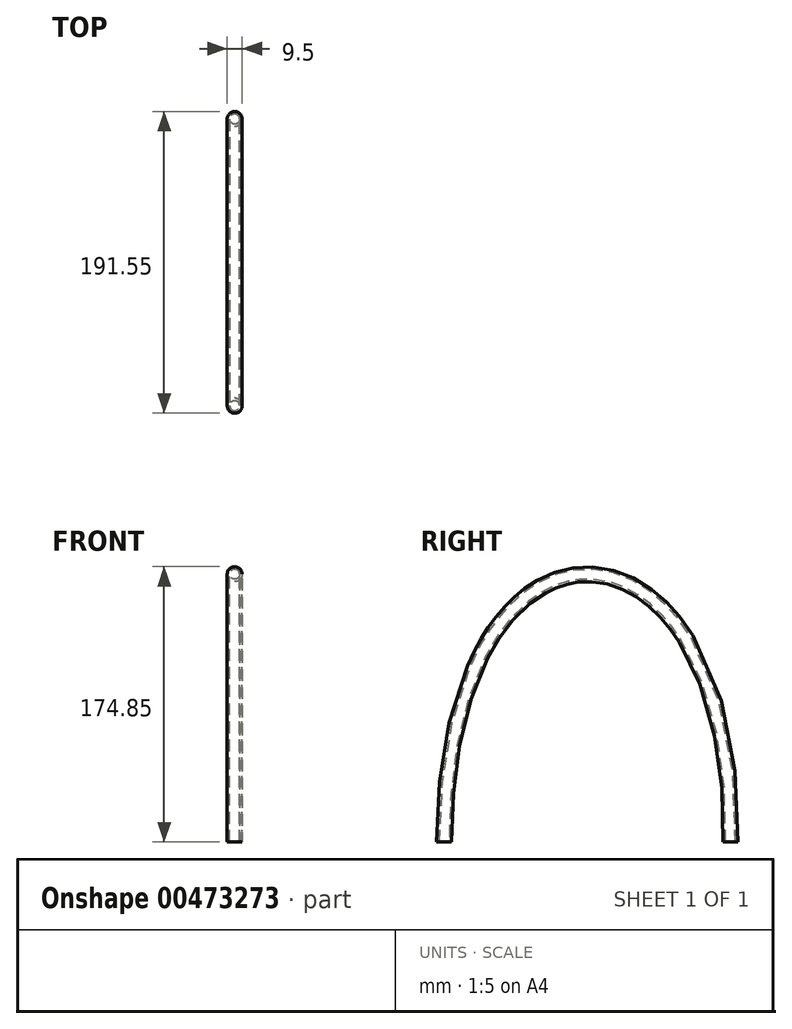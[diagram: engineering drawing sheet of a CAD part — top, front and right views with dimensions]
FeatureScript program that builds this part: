
annotation { "Feature Type Name" : "Feature", "Feature Type Description" : "" }
export const myFeature = defineFeature(function(context is Context, id is Id, definition is map)
    precondition{}
    {
        {
            var Q0;
            Q0=qCreatedBy(makeId("Top.planeOp"), FACE);
            var sketch = newSketch(context, id + "F0", { "sketchPlane" : qUnion([Q0])});
            skCircle(sketch, "E0", {"center": v(0, 0) * mm, "radius": 3.14 * mm});
            skCircle(sketch, "E1", {"center": v(0, 0) * mm, "radius": 4.75 * mm});
            skSolve(sketch);
        }
        {
            var Q0;
            Q0=qCreatedBy(makeId("Right.planeOp"), FACE);
            var sketch = newSketch(context, id + "F1", { "sketchPlane" : qUnion([Q0])});
            skPoint(sketch, "E2", {"position": v(181.97, 0) * mm});
            skFitSpline(sketch, "E3", {"points": [v(0, 0) * mm, v(181.97, 0) * mm], "startDerivative": vector(0, 695.04) * mm, "endDerivative": vector(-13.52, -664.76) * mm});
            skSolve(sketch);
        }
        {
            var Q0;
            Q0 = qSketchRegion(id + "F0", true);
            var Q1;
            Q1 = qConstructionFilter(qBodyType(qCreatedBy(id + "F1" ,EDGE), BodyType.WIRE), ConstructionObject.NO);
            sweep(context, id + "F2", {"profiles" : qUnion([Q0]), "path" : qUnion([Q1])});
        }
    });
